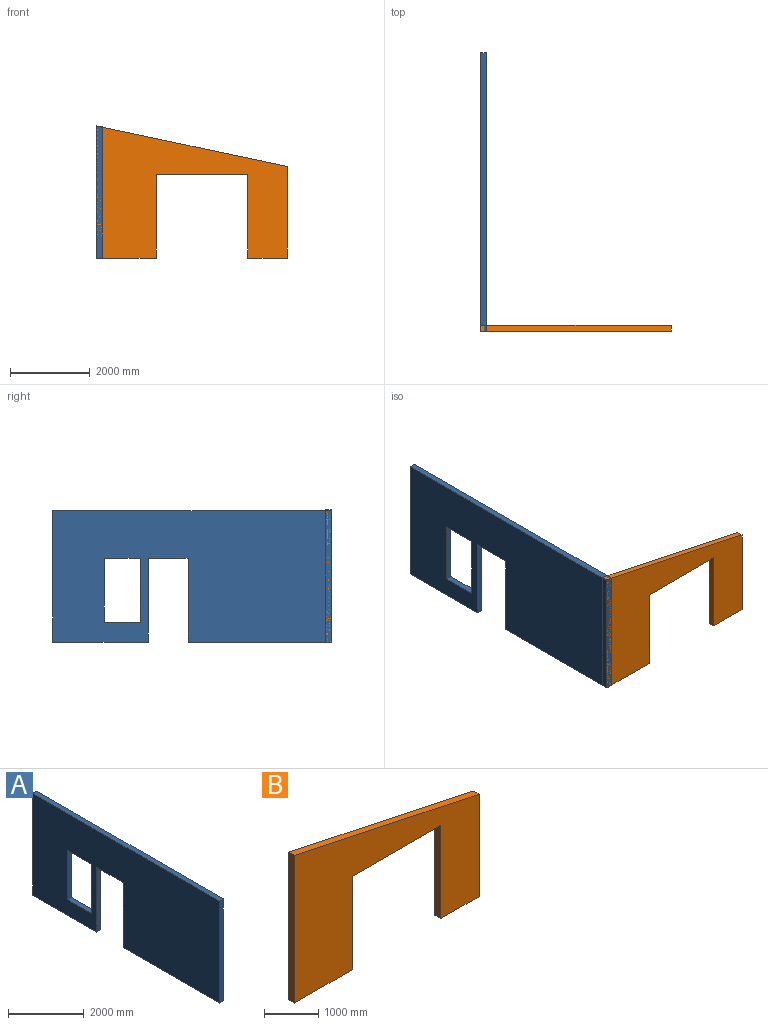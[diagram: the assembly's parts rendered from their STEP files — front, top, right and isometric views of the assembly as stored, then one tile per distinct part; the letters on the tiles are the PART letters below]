
ASSEMBLY  parts=2 mates=1
PART A: 14 faces, bbox 150x7000x3300 mm
  f0: plane 2400x150mm, normal (0,0,-1), area 360000mm2, adj f1,f7,f8,f9
  f1: plane 3300x150mm, normal (0,1,0), area 495000mm2, adj f0,f2,f8,f9
  f2: plane 7000x150mm, normal (0,0,1), area 1050000mm2, adj f1,f3,f8,f9
  f3: plane 3300x150mm, normal (0,-1,0), area 495000mm2, adj f2,f4,f8,f9
  f4: plane 3600x150mm, normal (0,0,-1), area 540000mm2, adj f3,f5,f8,f9
  f5: plane 2100x150mm, normal (0,1,0), area 315000mm2, adj f4,f6,f8,f9
  f6: plane 1000x150mm, normal (0,0,-1), area 150000mm2, adj f5,f7,f8,f9
  f7: plane 2100x150mm, normal (0,-1,0), area 315000mm2, adj f0,f6,f8,f9
  f8: plane 7000x3300mm, normal (-1,0,0), area 19560000mm2, adj f0,f1,f2,f3,f4,f5,f6,f7
  f9: plane 7000x3300mm, normal (1,0,0), area 19560000mm2, adj f0,f1,f2,f3,f4,f5,f6,f7
  f10: plane 1600x150mm, normal (0,1,0), area 240000mm2, adj f8,f9,f11,f13
  f11: plane 900x150mm, normal (0,0,1), area 135000mm2, adj f8,f9,f10,f12
  f12: plane 1600x150mm, normal (0,-1,0), area 240000mm2, adj f8,f9,f11,f13
  f13: plane 900x150mm, normal (0,0,-1), area 135000mm2, adj f8,f9,f10,f12
PART B: 10 faces, bbox 4800x150x3320.3 mm
  f0: plane 3320.27x150mm, normal (-1,0,0), area 498040.7mm2, adj f1,f7,f8,f9
  f1: plane 1500x150mm, normal (0,0,-1), area 225000mm2, adj f0,f2,f8,f9
  f2: plane 2100x150mm, normal (1,0,0), area 315000mm2, adj f1,f3,f8,f9
  f3: plane 2300x150mm, normal (0,0,-1), area 345000mm2, adj f2,f4,f8,f9
  f4: plane 2100x150mm, normal (-1,0,0), area 315000mm2, adj f3,f5,f8,f9
  f5: plane 1000x150mm, normal (0,0,-1), area 150000mm2, adj f4,f6,f8,f9
  f6: plane 2300x150mm, normal (1,0,0), area 345000mm2, adj f5,f7,f8,f9
  f7: plane 4800x1020.27mm, normal (0.21,0,0.98), area 736085.2mm2, adj f0,f6,f8,f9
  f8: plane 4800x3320.27mm, normal (0,1,0), area 8658651.6mm2, adj f0,f1,f2,f3,f4,f5,f6,f7
  f9: plane 4800x3320.27mm, normal (0,-1,0), area 8658651.6mm2, adj f0,f1,f2,f3,f4,f5,f6,f7
PLACE A t=(-8551.65,-206.6,604.29)mm
PLACE B t=(-3901.65,-206.6,604.29)mm
MATE fastened A.f4 <-> B.f1  axis (0,0,1) through (-8701.65,-206.6,604.29)mm
